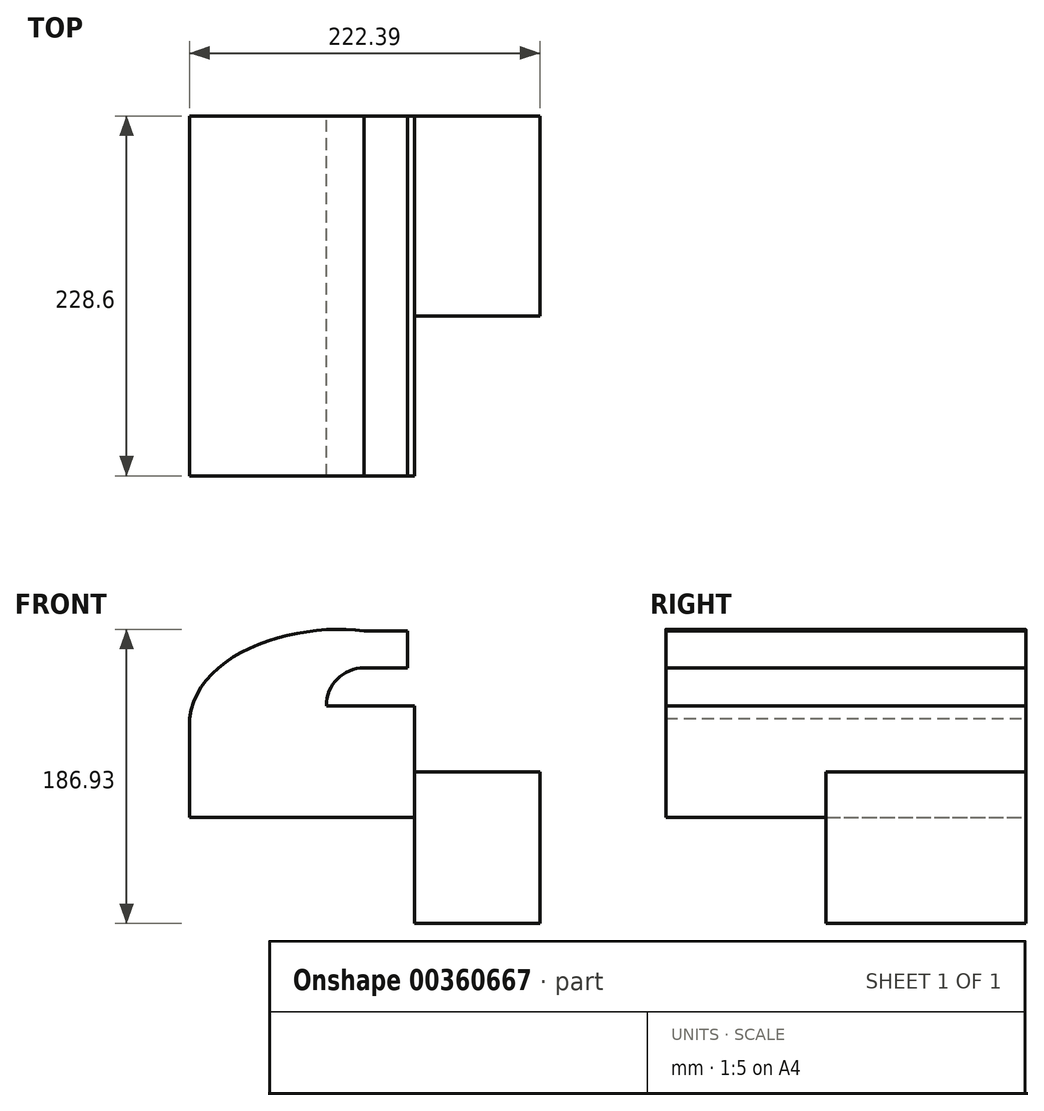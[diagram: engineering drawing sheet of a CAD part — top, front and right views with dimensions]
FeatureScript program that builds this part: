
annotation { "Feature Type Name" : "Feature", "Feature Type Description" : "" }
export const myFeature = defineFeature(function(context is Context, id is Id, definition is map)
    precondition{}
    {
        {
            var Q0;
            Q0=qCreatedBy(makeId("Front.planeOp"),FACE);
            var sketch = newSketch(context, id + "F0", { "sketchPlane" : qUnion([Q0])});
            skLineSegment(sketch, "E0.bottom", {"start": v(-35.14, -8.15) * mm, "end": v(-121.9, -8.15) * mm});
            skLineSegment(sketch, "E0.top", {"start": v(-35.14, 54.51) * mm, "end": v(-121.9, 54.51) * mm});
            skLineSegment(sketch, "E0.left", {"start": v(-35.14, -8.15) * mm, "end": v(-35.14, 54.51) * mm});
            skLineSegment(sketch, "E0.right", {"start": v(-121.9, -8.15) * mm, "end": v(-121.9, 54.51) * mm});
            skPoint(sketch, "E0.middle", {"position": v(-78.52, 23.18) * mm});
            skLineSegment(sketch, "E1.bottom", {"start": v(100.5, -4.53) * mm, "end": v(20.89, -4.53) * mm});
            skLineSegment(sketch, "E1.top", {"start": v(100.5, 20.69) * mm, "end": v(20.89, 20.69) * mm});
            skLineSegment(sketch, "E1.left", {"start": v(100.5, -4.53) * mm, "end": v(100.5, 20.69) * mm});
            skLineSegment(sketch, "E1.right", {"start": v(20.89, -4.53) * mm, "end": v(20.89, 20.69) * mm});
            skPoint(sketch, "E1.middle", {"position": v(60.69, 8.08) * mm});
            skLineSegment(sketch, "E2", {"start": v(-35.14, 54.51) * mm, "end": v(-35.14, 62.75) * mm});
            skArc(sketch, "E3", {"start": v(-35.14, 62.75) * mm, "mid": v(-28.1, 79.76) * mm, "end": v(-11.1, 86.8) * mm});
            skLineSegment(sketch, "E4", {"start": v(-11.1, 86.8) * mm, "end": v(16.35, 86.8) * mm});
            skLineSegment(sketch, "E5.0", {"start": v(-11.1, 110.3) * mm, "end": v(16.35, 110.3) * mm});
            skArc(sketch, "E5.1", {"start": v(-58.63, 62.75) * mm, "mid": v(-44.7, 96.37) * mm, "end": v(-11.1, 110.3) * mm});
            skLineSegment(sketch, "E5.2", {"start": v(-58.63, 41.18) * mm, "end": v(-58.63, 62.75) * mm});
            skLineSegment(sketch, "E6", {"start": v(16.35, 86.8) * mm, "end": v(16.35, 110.3) * mm});
            skFitSpline(sketch, "E7", {"points": [v(-121.9, 54.51) * mm, v(-11.1, 110.3) * mm], "startDerivative": vector(13.56, 127.92) * mm, "endDerivative": vector(129.5, -17.09) * mm});
            skSolve(sketch);
        }
        {
            var Q0;
            Q0 = qSketchRegion(id + "F0", true);
            extrude(context, id + "F1", {"entities" : qUnion([Q0]), "endBound" : BoundingType.SYMMETRIC, "depth" : 127 * mm});
        }
        {
            var Q0;
            Q0=makeQuery(id+"F1.opExtrude","CAP_FACE",FACE,{"disambiguationData":[OSD([sQuery(id+"F0.wireOp",EDGE,"E0.bottom"),sQuery(id+"F0.wireOp",EDGE,"E0.left"),sQuery(id+"F0.wireOp",EDGE,"E0.right"),sQuery(id+"F0.wireOp",EDGE,"E2"),sQuery(id+"F0.wireOp",EDGE,"E3"),sQuery(id+"F0.wireOp",EDGE,"E4"),sQuery(id+"F0.wireOp",EDGE,"E5.0"),sQuery(id+"F0.wireOp",EDGE,"E6"),sQuery(id+"F0.wireOp",EDGE,"E7")])],"isStart":false});
            extrude(context, id + "F2", {"entities" : qUnion([Q0]), "operationType" : NewBodyOperationType.ADD, "depth" : 101.6 * mm});
        }
        {
            var Q0;
            {var subQ0=sQuery(id+"F0.wireOp",EDGE,"E2");var subQ1=sQuery(id+"F0.wireOp",EDGE,"E0.left");Q0=makeQuery(id+"F2.boolean.opBoolean","MERGE",FACE,{"derivedFrom":[makeQuery(id+"F1.opExtrude","SWEPT_FACE",FACE,{"disambiguationData":[OSD([subQ1,subQ0])]}),makeQuery(id+"F2.opExtrude","SWEPT_FACE",FACE,{"disambiguationData":[OSD([subQ1,subQ0])]})]});}
            extrude(context, id + "F3", {"entities" : qUnion([Q0]), "operationType" : NewBodyOperationType.ADD, "depth" : 55.88 * mm});
        }
        {
            var Q0;
            Q0=makeQuery(id+"F1.opExtrude","SWEPT_FACE",FACE,{"disambiguationData":[OSD([sQuery(id+"F0.wireOp",EDGE,"E1.bottom")])]});
            var sketch = newSketch(context, id + "F4", { "sketchPlane" : qUnion([Q0])});
            skSolve(sketch);
        }
        {
            var Q0;
            {var subQ0=sQuery(id+"F0.wireOp",EDGE,"E1.bottom");Q0=makeQuery(id+"F4.imprint","IMPRINT",FACE,{"disambiguationData":[TD([[makeQuery(id+"F4.imprint","IMPRINT",EDGE,{"derivedFrom":makeQuery(id+"F1.opExtrude","CAP_EDGE",EDGE,{"disambiguationData":[OSD([subQ0])],"isStart":true})}),-1.0]])]});}
            extrude(context, id + "F5", {"entities" : qUnion([Q0]), "operationType" : NewBodyOperationType.ADD, "depth" : 71.12 * mm});
        }
    });
